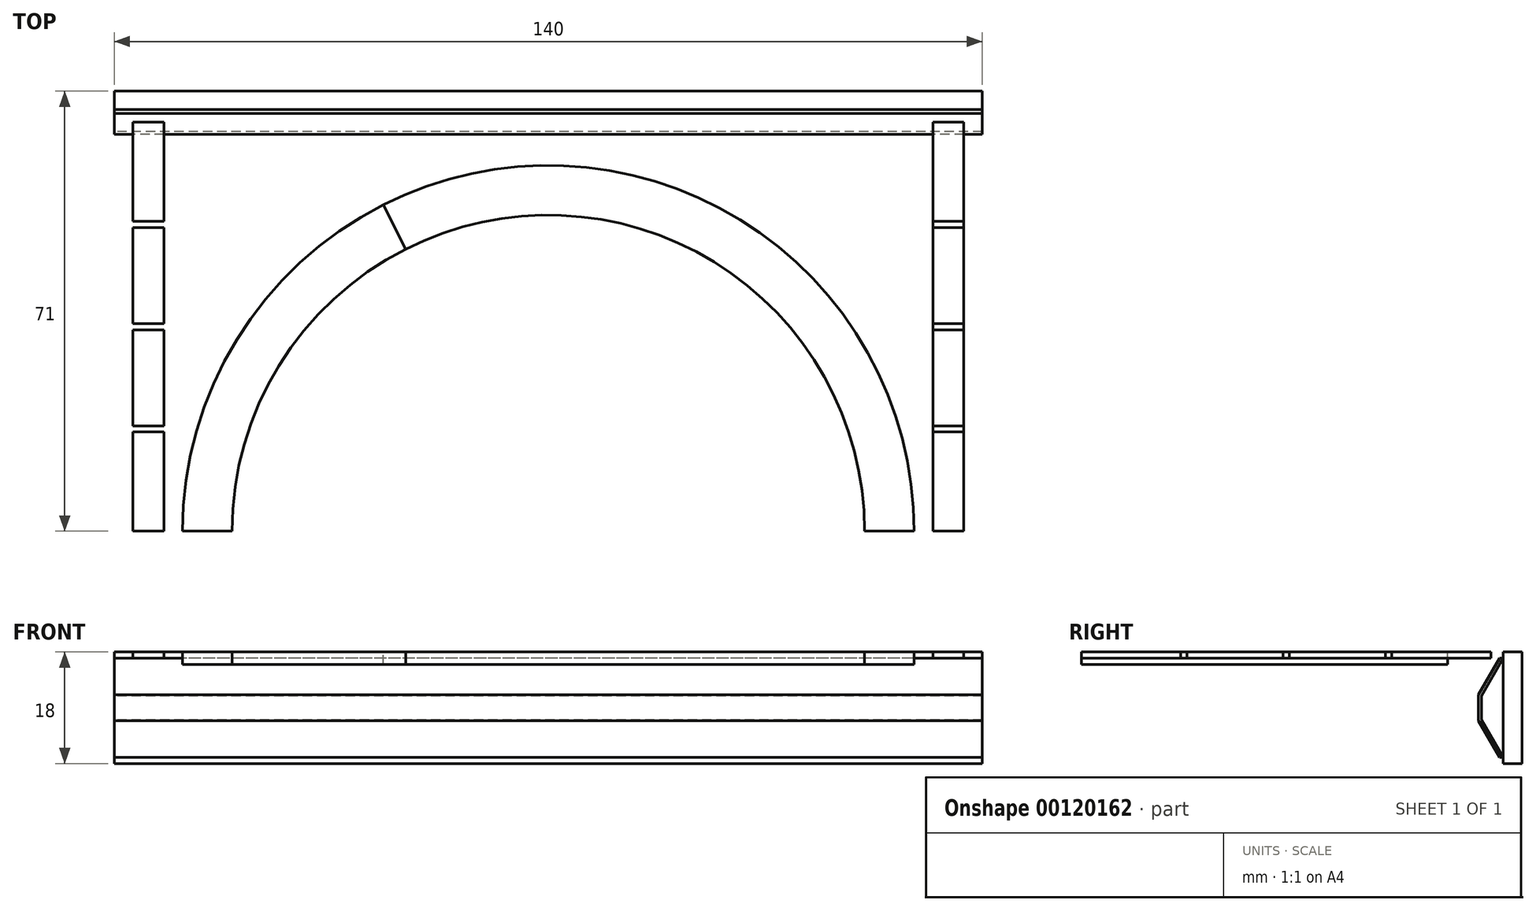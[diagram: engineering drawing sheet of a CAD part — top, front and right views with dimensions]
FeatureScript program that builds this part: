
annotation { "Feature Type Name" : "Feature", "Feature Type Description" : "" }
export const myFeature = defineFeature(function(context is Context, id is Id, definition is map)
    precondition{}
    {
        {
            var Q0;
            Q0=qCreatedBy(makeId("Top.planeOp"),FACE);
            var sketch = newSketch(context, id + "F0", { "sketchPlane" : qUnion([Q0])});
            skLineSegment(sketch, "E0.bottom", {"start": v(-70, 35) * mm, "end": v(70, 35) * mm});
            skLineSegment(sketch, "E0.top", {"start": v(-70, -35) * mm, "end": v(70, -35) * mm});
            skLineSegment(sketch, "E0.left", {"start": v(-70, 35) * mm, "end": v(-70, -35) * mm});
            skLineSegment(sketch, "E0.right", {"start": v(70, 35) * mm, "end": v(70, -35) * mm});
            skPoint(sketch, "E0.middle", {"position": v(0, 0) * mm});
            skLineSegment(sketch, "E1.bottom", {"start": v(-67, 33) * mm, "end": v(-62, 33) * mm});
            skLineSegment(sketch, "E1.top", {"start": v(-67, -33) * mm, "end": v(-62, -33) * mm});
            skLineSegment(sketch, "E1.left", {"start": v(-67, 33) * mm, "end": v(-67, -33) * mm});
            skLineSegment(sketch, "E1.right", {"start": v(-62, 33) * mm, "end": v(-62, -33) * mm});
            skLineSegment(sketch, "E2.MirrorCS", {"start": v(62, 33) * mm, "end": v(62, -33) * mm});
            skLineSegment(sketch, "E3.MirrorCS", {"start": v(67, 33) * mm, "end": v(62, 33) * mm});
            skLineSegment(sketch, "E4.MirrorCS", {"start": v(67, 33) * mm, "end": v(67, -33) * mm});
            skLineSegment(sketch, "E5.MirrorCS", {"start": v(67, -33) * mm, "end": v(62, -33) * mm});
            skPoint(sketch, "E6", {"position": v(-59, -33) * mm});
            skPoint(sketch, "E7.MirrorP", {"position": v(59, -33) * mm});
            skPoint(sketch, "E8", {"position": v(0, 26) * mm});
            skArc(sketch, "E9", {"start": v(59, -33) * mm, "mid": v(0, 26) * mm, "end": v(-59, -33) * mm});
            skArc(sketch, "E10.0", {"start": v(51, -33) * mm, "mid": v(0, 18) * mm, "end": v(-51, -33) * mm});
            skLineSegment(sketch, "E11", {"start": v(-59, -33) * mm, "end": v(-51, -33) * mm});
            skLineSegment(sketch, "E12", {"start": v(51, -33) * mm, "end": v(59, -33) * mm});
            skLineSegment(sketch, "E13.bottom", {"start": v(-29.63, 3.93) * mm, "end": v(29.63, 3.93) * mm});
            skLineSegment(sketch, "E13.top", {"start": v(-29.63, -33) * mm, "end": v(29.63, -33) * mm});
            skLineSegment(sketch, "E13.left", {"start": v(-29.63, 3.93) * mm, "end": v(-29.63, -33) * mm});
            skLineSegment(sketch, "E13.right", {"start": v(29.63, 3.93) * mm, "end": v(29.63, -33) * mm});
            skPoint(sketch, "E13.middle", {"position": v(0, -14.53) * mm});
            skLineSegment(sketch, "E14", {"start": v(-67, 0) * mm, "end": v(-62, 0) * mm});
            skLineSegment(sketch, "E15", {"start": v(-67, 16.5) * mm, "end": v(-62, 16.5) * mm});
            skLineSegment(sketch, "E16.bottom", {"start": v(-67, 17) * mm, "end": v(-62, 17) * mm});
            skLineSegment(sketch, "E16.top", {"start": v(-67, 16) * mm, "end": v(-62, 16) * mm});
            skLineSegment(sketch, "E16.left", {"start": v(-67, 17) * mm, "end": v(-67, 16) * mm});
            skLineSegment(sketch, "E16.right", {"start": v(-62, 17) * mm, "end": v(-62, 16) * mm});
            skLineSegment(sketch, "E17.bottom", {"start": v(-67, 0.5) * mm, "end": v(-62, 0.5) * mm});
            skLineSegment(sketch, "E17.top", {"start": v(-67, -0.5) * mm, "end": v(-62, -0.5) * mm});
            skLineSegment(sketch, "E17.left", {"start": v(-67, 0.5) * mm, "end": v(-67, -0.5) * mm});
            skLineSegment(sketch, "E17.right", {"start": v(-62, 0.5) * mm, "end": v(-62, -0.5) * mm});
            skLineSegment(sketch, "E18.MirrorCS", {"start": v(-67, -17) * mm, "end": v(-62, -17) * mm});
            skLineSegment(sketch, "E19.MirrorCS", {"start": v(-67, -16) * mm, "end": v(-62, -16) * mm});
            skLineSegment(sketch, "E20.MirrorCS", {"start": v(67, 17) * mm, "end": v(62, 17) * mm});
            skLineSegment(sketch, "E21.MirrorCS", {"start": v(67, 16) * mm, "end": v(62, 16) * mm});
            skLineSegment(sketch, "E22.MirrorCS", {"start": v(67, 0.5) * mm, "end": v(62, 0.5) * mm});
            skLineSegment(sketch, "E23.MirrorCS", {"start": v(67, -0.5) * mm, "end": v(62, -0.5) * mm});
            skLineSegment(sketch, "E24.MirrorCS", {"start": v(67, -16) * mm, "end": v(62, -16) * mm});
            skLineSegment(sketch, "E25.MirrorCS", {"start": v(67, -17) * mm, "end": v(62, -17) * mm});
            skLineSegment(sketch, "E26", {"start": v(-26.63, 19.65) * mm, "end": v(-16.72, 24.66) * mm});
            skLineSegment(sketch, "E27", {"start": v(-26.63, 19.65) * mm, "end": v(-23.02, 12.51) * mm});
            skSolve(sketch);
        }
        {
            var Q0;
            {var subQ0=sQuery(id+"F0.wireOp",EDGE,"E1.bottom");Q0=makeQuery(id+"F0.imprint","IMPRINT",FACE,{"disambiguationData":[TD([[makeQuery(id+"F0.imprint","IMPRINT",EDGE,{"derivedFrom":subQ0}),-1.0]])]});}
            var Q1;
            {var subQ0=sQuery(id+"F0.wireOp",EDGE,"E16.top");Q1=makeQuery(id+"F0.imprint","IMPRINT",FACE,{"disambiguationData":[TD([[makeQuery(id+"F0.imprint","IMPRINT",EDGE,{"derivedFrom":subQ0}),-1.0]])]});}
            var Q2;
            {var subQ0=sQuery(id+"F0.wireOp",EDGE,"E17.top");Q2=makeQuery(id+"F0.imprint","IMPRINT",FACE,{"disambiguationData":[TD([[makeQuery(id+"F0.imprint","IMPRINT",EDGE,{"derivedFrom":subQ0}),-1.0]])]});}
            var Q3;
            {var subQ0=sQuery(id+"F0.wireOp",EDGE,"E1.top");Q3=makeQuery(id+"F0.imprint","IMPRINT",FACE,{"disambiguationData":[TD([[makeQuery(id+"F0.imprint","IMPRINT",EDGE,{"derivedFrom":subQ0}),1.0]])]});}
            var Q4;
            {var subQ0=sQuery(id+"F0.wireOp",EDGE,"E3.MirrorCS");Q4=makeQuery(id+"F0.imprint","IMPRINT",FACE,{"disambiguationData":[TD([[makeQuery(id+"F0.imprint","IMPRINT",EDGE,{"derivedFrom":subQ0}),1.0]])]});}
            var Q5;
            {var subQ0=sQuery(id+"F0.wireOp",EDGE,"E21.MirrorCS");Q5=makeQuery(id+"F0.imprint","IMPRINT",FACE,{"disambiguationData":[TD([[makeQuery(id+"F0.imprint","IMPRINT",EDGE,{"derivedFrom":subQ0}),1.0]])]});}
            var Q6;
            {var subQ0=sQuery(id+"F0.wireOp",EDGE,"E23.MirrorCS");Q6=makeQuery(id+"F0.imprint","IMPRINT",FACE,{"disambiguationData":[TD([[makeQuery(id+"F0.imprint","IMPRINT",EDGE,{"derivedFrom":subQ0}),1.0]])]});}
            var Q7;
            {var subQ0=sQuery(id+"F0.wireOp",EDGE,"E5.MirrorCS");Q7=makeQuery(id+"F0.imprint","IMPRINT",FACE,{"disambiguationData":[TD([[makeQuery(id+"F0.imprint","IMPRINT",EDGE,{"derivedFrom":subQ0}),-1.0]])]});}
            extrude(context, id + "F1", {"entities" : qUnion([Q0, Q1, Q2, Q3, Q4, Q5, Q6, Q7]), "oppositeDirection" : true, "depth" : 1 * mm});
        }
        {
            var Q0;
            {var subQ0=sQuery(id+"F0.wireOp",EDGE,"E11");Q0=makeQuery(id+"F0.imprint","IMPRINT",FACE,{"disambiguationData":[TD([[makeQuery(id+"F0.imprint","IMPRINT",EDGE,{"derivedFrom":subQ0}),1.0]])]});}
            extrude(context, id + "F2", {"entities" : qUnion([Q0]), "oppositeDirection" : true, "depth" : 2 * mm});
        }
        {
            var Q0;
            {var subQ0=sQuery(id+"F0.wireOp",EDGE,"E3.MirrorCS");Q0=makeQuery(id+"F0.imprint","IMPRINT",FACE,{"disambiguationData":[TD([[makeQuery(id+"F0.imprint","IMPRINT",EDGE,{"derivedFrom":subQ0}),1.0]])]});}
            var Q1;
            {var subQ0=sQuery(id+"F0.wireOp",EDGE,"E20.MirrorCS");Q1=makeQuery(id+"F0.imprint","IMPRINT",FACE,{"disambiguationData":[TD([[makeQuery(id+"F0.imprint","IMPRINT",EDGE,{"derivedFrom":subQ0}),1.0]])]});}
            var Q2;
            {var subQ0=sQuery(id+"F0.wireOp",EDGE,"E21.MirrorCS");Q2=makeQuery(id+"F0.imprint","IMPRINT",FACE,{"disambiguationData":[TD([[makeQuery(id+"F0.imprint","IMPRINT",EDGE,{"derivedFrom":subQ0}),1.0]])]});}
            var Q3;
            {var subQ0=sQuery(id+"F0.wireOp",EDGE,"E22.MirrorCS");Q3=makeQuery(id+"F0.imprint","IMPRINT",FACE,{"disambiguationData":[TD([[makeQuery(id+"F0.imprint","IMPRINT",EDGE,{"derivedFrom":subQ0}),1.0]])]});}
            var Q4;
            {var subQ0=sQuery(id+"F0.wireOp",EDGE,"E23.MirrorCS");Q4=makeQuery(id+"F0.imprint","IMPRINT",FACE,{"disambiguationData":[TD([[makeQuery(id+"F0.imprint","IMPRINT",EDGE,{"derivedFrom":subQ0}),1.0]])]});}
            var Q5;
            {var subQ0=sQuery(id+"F0.wireOp",EDGE,"E24.MirrorCS");Q5=makeQuery(id+"F0.imprint","IMPRINT",FACE,{"disambiguationData":[TD([[makeQuery(id+"F0.imprint","IMPRINT",EDGE,{"derivedFrom":subQ0}),1.0]])]});}
            var Q6;
            {var subQ0=sQuery(id+"F0.wireOp",EDGE,"E5.MirrorCS");Q6=makeQuery(id+"F0.imprint","IMPRINT",FACE,{"disambiguationData":[TD([[makeQuery(id+"F0.imprint","IMPRINT",EDGE,{"derivedFrom":subQ0}),-1.0]])]});}
            extrude(context, id + "F3", {"entities" : qUnion([Q0, Q1, Q2, Q3, Q4, Q5, Q6]), "oppositeDirection" : true, "depth" : 1 * mm});
        }
        {
            var Q0;
            {var subQ0=sQuery(id+"F0.wireOp",EDGE,"E12");Q0=makeQuery(id+"F0.imprint","IMPRINT",FACE,{"disambiguationData":[TD([[makeQuery(id+"F0.imprint","IMPRINT",EDGE,{"derivedFrom":subQ0}),1.0]])]});}
            extrude(context, id + "F4", {"entities" : qUnion([Q0]), "oppositeDirection" : true, "depth" : 2 * mm});
        }
        {
            var Q0;
            Q0=qCreatedBy(makeId("Right.planeOp"),FACE);
            var sketch = newSketch(context, id + "F5", { "sketchPlane" : qUnion([Q0])});
            skLineSegment(sketch, "E28", {"start": v(35, 0) * mm, "end": v(35, -18) * mm});
            skPoint(sketch, "E29", {"position": v(35, -9) * mm});
            skLineSegment(sketch, "E30", {"start": v(35, -9) * mm, "end": v(24.6, -9) * mm});
            skLineSegment(sketch, "E31", {"start": v(35, 0) * mm, "end": v(29.8, -9) * mm});
            skLineSegment(sketch, "E32", {"start": v(29.8, -9) * mm, "end": v(35, -18) * mm});
            skLineSegment(sketch, "E33", {"start": v(31, -6.92) * mm, "end": v(31, -11.08) * mm});
            skLineSegment(sketch, "E34", {"start": v(34.42, -1) * mm, "end": v(35, -1) * mm});
            skLineSegment(sketch, "E35.MirrorCS", {"start": v(34.42, -17) * mm, "end": v(35, -17) * mm});
            skLineSegment(sketch, "E36.0", {"start": v(38, 0) * mm, "end": v(38, -18) * mm});
            skLineSegment(sketch, "E37.0", {"start": v(35.43, -0.25) * mm, "end": v(30.38, -9) * mm});
            skLineSegment(sketch, "E38.MirrorCS", {"start": v(35.43, -17.75) * mm, "end": v(30.38, -9) * mm});
            skLineSegment(sketch, "E39", {"start": v(35, 0) * mm, "end": v(38, 0) * mm});
            skLineSegment(sketch, "E40", {"start": v(35, -18) * mm, "end": v(38, -18) * mm});
            skLineSegment(sketch, "E41.0", {"start": v(31.5, -6.92) * mm, "end": v(31.5, -11.08) * mm});
            skSolve(sketch);
        }
        {
            var Q0;
            {var subQ5=sQuery(id+"F5.wireOp",EDGE,"E34");Q0=makeQuery(id+"F5.imprint","IMPRINT",FACE,{"disambiguationData":[TD([[makeQuery(id+"F5.imprint","IMPRINT",EDGE,{"derivedFrom":subQ5}),-1.0]])]});}
            var Q1;
            {var subQ5=sQuery(id+"F5.wireOp",EDGE,"E35.MirrorCS");Q1=makeQuery(id+"F5.imprint","IMPRINT",FACE,{"disambiguationData":[TD([[makeQuery(id+"F5.imprint","IMPRINT",EDGE,{"derivedFrom":subQ5}),1.0]])]});}
            var Q2;
            Q2=makeQuery(id+"F5.imprint","IMPRINT",FACE,{"disambiguationData":[TD([[makeQuery(id+"F5.imprint","IMPRINT",EDGE,{"derivedFrom":sQuery(id+"F5.wireOp",EDGE,"E36.0")}),-1.0]])]});
            var Q3;
            {var subQ0=sQuery(id+"F5.wireOp",EDGE,"E41.0");var subQ1=sQuery(id+"F5.wireOp",EDGE,"E30");var subQ2=makeQuery(id+"F5.imprint","INTERSECT",VERTEX,{"derivedFrom":[subQ1,subQ0]});Q3=makeQuery(id+"F5.imprint","IMPRINT",FACE,{"disambiguationData":[TD([[makeQuery(id+"F5.imprint","IMPRINT",EDGE,{"disambiguationData":[TD([[subQ2,-1.0]])],"derivedFrom":subQ1}),1.0]])]});}
            var Q4;
            {var subQ0=sQuery(id+"F5.wireOp",EDGE,"E41.0");var subQ1=sQuery(id+"F5.wireOp",EDGE,"E30");var subQ2=makeQuery(id+"F5.imprint","INTERSECT",VERTEX,{"derivedFrom":[subQ1,subQ0]});Q4=makeQuery(id+"F5.imprint","IMPRINT",FACE,{"disambiguationData":[TD([[makeQuery(id+"F5.imprint","IMPRINT",EDGE,{"disambiguationData":[TD([[subQ2,-1.0]])],"derivedFrom":subQ1}),-1.0]])]});}
            extrude(context, id + "F6", {"entities" : qUnion([Q0, Q1, Q2, Q3, Q4]), "endBound" : BoundingType.SYMMETRIC, "depth" : 140 * mm});
        }
    });
